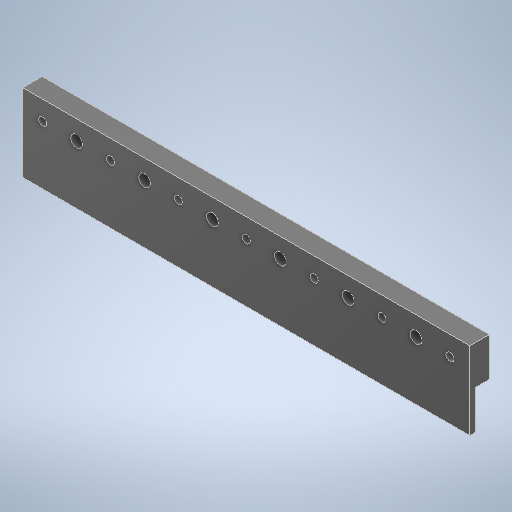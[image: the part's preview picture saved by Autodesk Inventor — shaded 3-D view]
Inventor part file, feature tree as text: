
AUTODESK INVENTOR PART (.ipt)
format: ipt  version: 2025.1 (Build 291241020, 241B)  size: 465,408 bytes
history: native  units: mm
features: sketch x5, extrude x3, hole x2, pattern_linear x2, other x2, chamfer x1, reference x1
ambient origin geometry x8: Origin, YZ Plane, XZ Plane, XY Plane, X Axis, Y Axis, Z Axis, Center Point
bodies: Solid1 (feature_tree)
feature tree (16):
  extrude  "Extrusion1"  Depth=20.0mm
  sketch  "Sketch2"  dims[d2=3.0mm d3=0.0mm d31=10.0mm]
  extrude  "Extrusion3"  Depth=10.0mm
  hole  "Hole3"  [1 undecoded]
  hole  "Hole2"  [1 undecoded]
  pattern_linear  "Rectangular Pattern2"  Spacing1=10.0mm  [1 undecoded]
  pattern_linear  "Rectangular Pattern3"  Count1=6 Spacing1=34.925mm
  chamfer  "Chamfer1"  Distance=10.0mm
  extrude  "Extrusion4"  Depth=10.0mm TaperAngle=45.0deg
  sketch  "Sketch1"  dims[d0=230.0mm d1=20.0mm]
  reference  "Reference1"
  sketch  "Sketch5"  dims[d32=20.0mm d33=10.0mm d34=0.0mm]
  sketch  "Sketch6"  dims[d35=27.6875mm]
  sketch  "Sketch7"  dims[d39=6.0mm d40=6.0mm d41=4.0mm d42=2.0mm d43=90.0deg d44=8.0mm d45=20.594885mm d47=34.925mm d51=10.0mm d52=4.1mm d53=6.0mm d54=4.0mm d55=2.0mm d56=90.0deg d57=6.0mm d58=0.0mm d59=60.0mm d61=34.925mm d62=10.0mm d63=2.0mm d64=2.0mm d65=45.0deg d66=5.0mm d67=0.0mm d68=0.0mm d73=10.225mm d74=70.0mm d76=34.925mm d77=0.5mm d78=0.872665mm d79=0.5mm d80=0.872665mm]
  other  "MagDrop4.iam"
  other  "Connect4_RACK:1"
note: 3 required parameter values undecoded (feature->parameter linkage not recoverable at this tier; creation-order binding heuristic only, values carry confidence <= 0.55)
